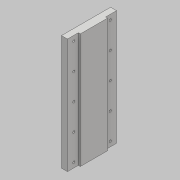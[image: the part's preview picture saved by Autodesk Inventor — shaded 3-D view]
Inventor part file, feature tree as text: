
AUTODESK INVENTOR PART (.ipt)
format: ipt  version: 2018 (Build 220112000, 112)  size: 118,272 bytes
history: native  units: mm
features: sketch x3, other x2, extrude x2, hole x1, chamfer x1, pattern_linear x1, plane x1, mirror x1
ambient origin geometry x8: Origin, YZ Plane, XZ Plane, XY Plane, X Axis, Y Axis, Z Axis, Center Point
bodies: Body1 (feature_tree)
feature tree (12):
  other  "實體1"
  extrude  "擠出1"  Depth=248.0mm
  extrude  "擠出2"  Depth=580.0mm
  hole  "孔1"  [1 undecoded]
  other  "刪除面1"
  chamfer  "倒角1"  Distance=580.0mm
  pattern_linear  "矩形陣列1"  Spacing1=138.0mm  [1 undecoded]
  plane  "工作平面1"
  mirror  "鏡射1"
  sketch  "草圖1"
  sketch  "草圖2"
  sketch  "草圖3"
note: 2 required parameter values undecoded (feature->parameter linkage not recoverable at this tier; creation-order binding heuristic only, values carry confidence <= 0.55)
